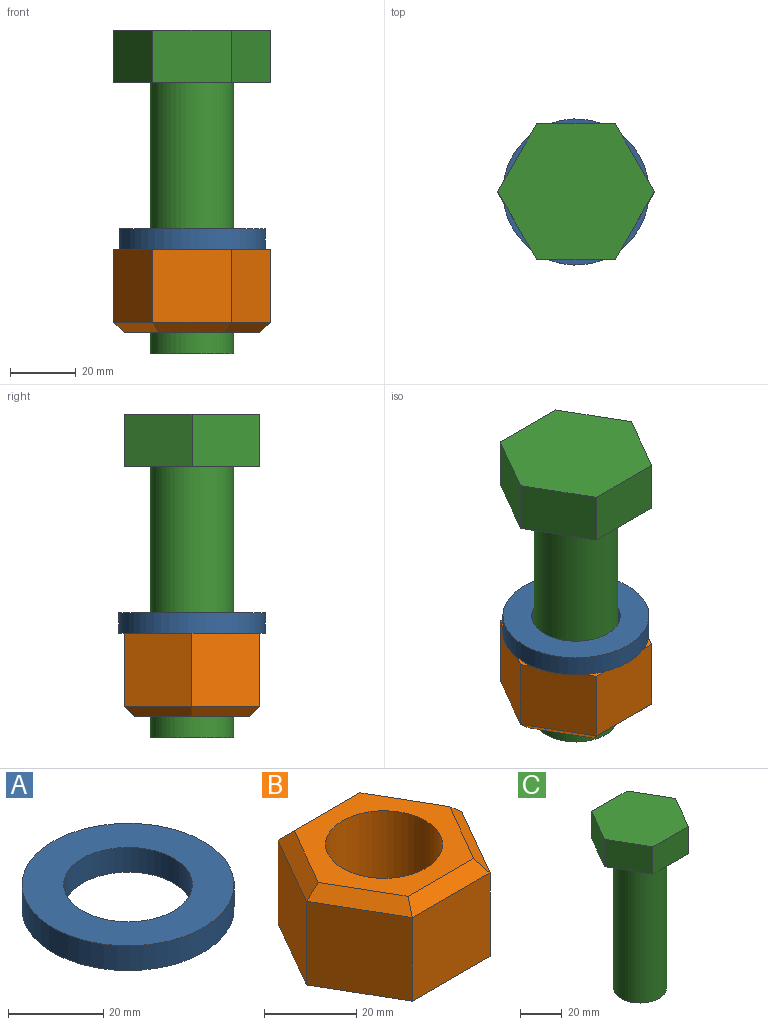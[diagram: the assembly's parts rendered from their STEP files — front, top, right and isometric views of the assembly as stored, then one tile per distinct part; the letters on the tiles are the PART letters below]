
ASSEMBLY  parts=3 mates=2
PART A: 4 faces, bbox 44.5x44.5x6.4 mm
  f0: cylinder r=13.49mm len=26.99mm, axis (0,0,-1), area 538.4mm2, adj f2,f3
  f1: cylinder r=22.23mm len=44.45mm, axis (0,0,-1), area 886.7mm2, adj f2,f3
  f2: plane 44.45x44.45mm, normal (0,0,1), area 979.8mm2, adj f0,f1
  f3: plane 44.45x44.45mm, normal (0,0,-1), area 979.8mm2, adj f0,f1
PART B: 15 faces, bbox 47.7x41.3x25.4 mm
  f0: plane 22.23x20.64mm, normal (-0.87,0.5,0), area 529.6mm2, adj f1,f6,f8,f9
  f1: plane 22.23x20.64mm, normal (-0.87,-0.5,0), area 529.6mm2, adj f0,f2,f8,f11
  f2: plane 23.83x22.23mm, normal (0,-1,0), area 529.6mm2, adj f1,f3,f8,f13
  f3: plane 22.23x20.64mm, normal (0.87,-0.5,0), area 529.6mm2, adj f2,f4,f8,f14
  f4: plane 22.23x20.64mm, normal (0.87,0.5,0), area 529.6mm2, adj f3,f6,f8,f12
  f5: cylinder r=12.7mm len=25.4mm, axis (0,0,-1), area 2026.8mm2, adj f7,f8
  f6: plane 23.83x22.23mm, normal (0,1,0), area 529.6mm2, adj f0,f4,f8,f10
  f7: plane 40.33x34.93mm, normal (0,0,1), area 549.6mm2, adj f5,f9,f10,f11,f12,f13,f14
  f8: plane 47.66x41.28mm, normal (0,0,-1), area 968.7mm2, adj f0,f1,f2,f3,f4,f5,f6
  f9: plane 20.64x13.75mm, normal (-0.61,0.35,0.71), area 98.8mm2, adj f0,f7,f10,f11
  f10: plane 23.83x3.18mm, normal (0,0.71,0.71), area 98.8mm2, adj f6,f7,f9,f12
  f11: plane 20.64x13.75mm, normal (-0.61,-0.35,0.71), area 98.8mm2, adj f1,f7,f9,f13
  f12: plane 20.64x13.75mm, normal (0.61,0.35,0.71), area 98.8mm2, adj f4,f7,f10,f14
  f13: plane 23.83x3.18mm, normal (0,-0.71,0.71), area 98.8mm2, adj f2,f7,f11,f14
  f14: plane 20.64x13.75mm, normal (0.61,-0.35,0.71), area 98.8mm2, adj f3,f7,f12,f13
PART C: 10 faces, bbox 47.7x41.3x98.4 mm
  f0: cylinder r=12.7mm len=82.55mm, axis (0,0,1), area 6587.2mm2, adj f1,f9
  f1: plane 25.4x25.4mm, normal (0,0,-1), area 506.7mm2, adj f0
  f2: plane 20.64x15.88mm, normal (-0.87,0.5,0), area 378.3mm2, adj f3,f7,f8,f9
  f3: plane 20.64x15.88mm, normal (-0.87,-0.5,0), area 378.3mm2, adj f2,f4,f8,f9
  f4: plane 23.83x15.88mm, normal (0,-1,0), area 378.3mm2, adj f3,f5,f8,f9
  f5: plane 20.64x15.88mm, normal (0.87,-0.5,0), area 378.3mm2, adj f4,f6,f8,f9
  f6: plane 20.64x15.88mm, normal (0.87,0.5,0), area 378.3mm2, adj f5,f7,f8,f9
  f7: plane 23.83x15.88mm, normal (0,1,0), area 378.3mm2, adj f2,f6,f8,f9
  f8: plane 47.66x41.28mm, normal (0,0,1), area 1475.4mm2, adj f2,f3,f4,f5,f6,f7
  f9: plane 47.66x41.28mm, normal (0,0,-1), area 968.7mm2, adj f0,f2,f3,f4,f5,f6,f7
PLACE A rot(axis=(1,0,0),180deg) t=(-11.47,-9.24,-22)mm
PLACE B rot(axis=(1,0,0),180deg) t=(-11.47,-9.24,-28.35)mm
PLACE C t=(-11.47,-9.24,22.45)mm
MATE fastened B.f5 <-> C.f0  axis (0,0,-1) through (-11.47,-9.24,-53.75)mm
MATE fastened A.f0 <-> B.f5  axis (0,0,-1) through (-11.47,-9.24,-28.35)mm
